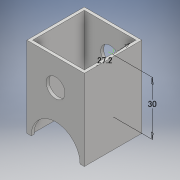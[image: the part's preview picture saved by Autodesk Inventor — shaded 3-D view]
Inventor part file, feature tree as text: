
AUTODESK INVENTOR PART (.ipt)
format: ipt  version: 2018 (Build 220112000, 112)  size: 122,368 bytes
history: native  units: mm
features: sketch x4, extrude x2, other x1, hole x1
ambient origin geometry x8: Origin, YZ Plane, XZ Plane, XY Plane, X Axis, Y Axis, Z Axis, Center Point
bodies: Body1 (feature_tree)
feature tree (8):
  other  "ソリッド1"
  extrude  "押し出し1"  Depth=32.0mm
  extrude  "押し出し2"  Depth=32.0mm
  hole  "穴1"  [1 undecoded]
  sketch  "スケッチ4"
  sketch  "スケッチ1"
  sketch  "スケッチ2"
  sketch  "スケッチ3"
note: 1 required parameter value undecoded (feature->parameter linkage not recoverable at this tier; creation-order binding heuristic only, values carry confidence <= 0.55)
